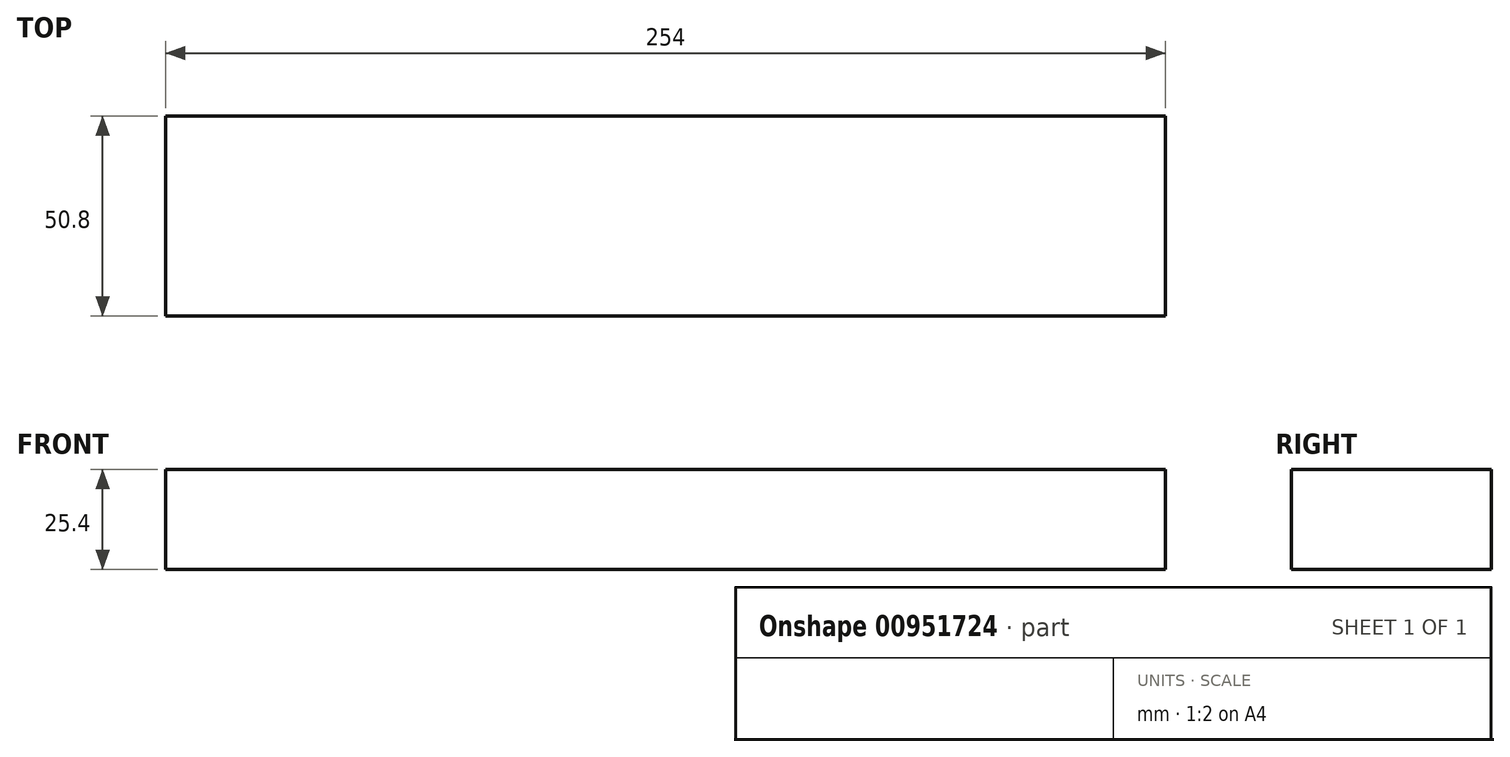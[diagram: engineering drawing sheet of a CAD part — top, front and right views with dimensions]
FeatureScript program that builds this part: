
annotation { "Feature Type Name" : "Feature", "Feature Type Description" : "" }
export const myFeature = defineFeature(function(context is Context, id is Id, definition is map)
    precondition{}
    {
        {
            var Q0;
            Q0=qCreatedBy(makeId("Top.planeOp"),FACE);
            var sketch = newSketch(context, id + "F0", { "sketchPlane" : qUnion([Q0])});
            skLineSegment(sketch, "E0.bottom", {"start": v(0, 0) * mm, "end": v(254, 0) * mm});
            skLineSegment(sketch, "E0.top", {"start": v(0, 50.8) * mm, "end": v(254, 50.8) * mm});
            skLineSegment(sketch, "E0.left", {"start": v(0, 0) * mm, "end": v(0, 50.8) * mm});
            skLineSegment(sketch, "E0.right", {"start": v(254, 0) * mm, "end": v(254, 50.8) * mm});
            skSolve(sketch);
        }
        {
            var Q0;
            Q0 = qSketchRegion(id + "F0", true);
            extrude(context, id + "F1", {"entities" : qUnion([Q0]), "oppositeDirection" : true, "depth" : 25.4 * mm, "offsetDistance" : 25.4 * mm});
        }
    });
